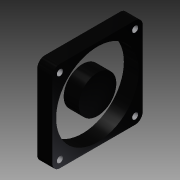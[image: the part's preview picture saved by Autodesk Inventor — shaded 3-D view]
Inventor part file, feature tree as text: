
AUTODESK INVENTOR PART (.ipt)
format: ipt  version: 2013 (Build 170138000, 138)  size: 131,072 bytes
history: native  units: mm
features: extrude x1, sketch x1
ambient origin geometry x8: Origin, YZ Plane, XZ Plane, XY Plane, X Axis, Y Axis, Z Axis, Center Point
bodies: Solid1 (feature_tree)
feature tree (2):
  extrude  "Extrusion1"  Depth=60.0mm
  sketch  "Sketch1"  dims[d0=60.0mm d2=60.0mm d3=5.0mm d4=5.0mm d5=4.0mm d6=4.0mm d7=4.0mm d8=4.0mm d9=30.0mm d10=30.0mm d11=55.0mm d12=10.0mm d13=0.0mm]
